# Revit family: efg_egg-20_60ms(t)b2_60Hz
name_source: partatom
category: 機械設備
units: mm (PartAtom-declared; Revit-internal decimal feet)

## family parameters
OmniClass タイトル = Industrial Ventilating Equipment
OmniClass 番号 = 23.75.35.21.17
パーツ タイプ = 標準
ロード時にボイドで切り取り = はい
丸型コネクタ寸法 = 直径を使用
作業面ベース = いいえ
共有 = いいえ
常に垂直 = はい
部屋計算ポイント = はい

## types (7) — shared parameters
IfcExportAs = IfcFanType
IfcExportType = TUBEAXIAL
MID風量 = 0.0 m³/h
OmniClassCode = 23-33 31 19 11 17
URL = https://www.mitsubishielectric.co.jp
Uniclass2015Code = Pr_65_67_29_67
Uniclass2015Title = Propeller fans
Uniclass2015Version = Systems v1.9
ファンの種類 = 軸流羽根
仕様書バージョン = Version1.0
企業コード = 108420
分類コード = 50052503100110
周波数 = 60 Hz
呼称 = 有圧扇
法定耐用年数 = 15
製品リリース年月 = 2022年6月1日
製品出荷対象 = 国内
製造元 = 三菱電機株式会社
設置方法 = 壁付
説明 = 業務用有圧換気扇 店舗用 メッシュタイプ 排気形
負荷分類 = 3_ファン類
運転質量 = 0.00 kg

## per-type parameters (varying)
| type | D1 | Depth | H1 | Height | MAX風量 | MIN風量 | W1 | Width | 価格 | 極 | 極数 | 消費電力 | 番手 | 相 | 製品質量 | 質量 | 電動機出力 | 電圧 |
| EFG-25MSB2 | 155  [stored 0.50853 ft] | 247 | 294  [stored 0.964567 ft] | 374  [stored 1.22703 ft] | 1130.0 m³/h | 870.0 m³/h | 294  [stored 0.964567 ft] | 379  [stored 1.24344 ft] | 68600 $ | 4 | 2 | 41 W | ∅250 | 1 | 6.10 kg | 7.32 kg | 25 W | 100 V |
| EFG-30MSB2 | 155  [stored 0.50853 ft] | 272 | 344  [stored 1.12861 ft] | 424  [stored 1.39108 ft] | 1720.0 m³/h | 1200.0 m³/h | 344  [stored 1.12861 ft] | 429  [stored 1.40748 ft] | 83500 $ | 4 | 2 | 61 W | ∅300 | 1 | 7.70 kg | 9.24 kg | 50 W | 100 V |
| EFG-35MSB2 | 155  [stored 0.50853 ft] | 277  [stored 0.908793 ft] | 399  [stored 1.30906 ft] | 479  [stored 1.57152 ft] | 2470.0 m³/h | 1810.0 m³/h | 399  [stored 1.30906 ft] | 484  [stored 1.58793 ft] | 121000 $ | 4 | 2 | 110 W | ∅350 | 1 | 10.60 kg | 12.72 kg | 100 W | 100 V |
| EFG-40MSB2 | 159  [stored 0.521654 ft] | 343  [stored 1.12533 ft] | 423  [stored 1.3878 ft] | 518  [stored 1.69948 ft] | 3460.0 m³/h | 2600.0 m³/h | 423  [stored 1.3878 ft] | 520  [stored 1.70604 ft] | 156000 $ | 4 | 2 | 177 W | ∅400 | 1 | 17.10 kg | 20.52 kg | 150 W | 100 V |
| EFG-40MSTB2 | 159  [stored 0.521654 ft] | 343  [stored 1.12533 ft] | 423  [stored 1.3878 ft] | 518  [stored 1.69948 ft] | 3420.0 m³/h | 0.0 m³/h | 423  [stored 1.3878 ft] | 520  [stored 1.70604 ft] | 156000 $ | 4 | 3 | 164 W | ∅400 | 3 | 16.90 kg | 20.28 kg | 150 W | 200 V |
| EGG-50MSTB2 | 189  [stored 0.620079 ft] | 413  [stored 1.35499 ft] | 524  [stored 1.71916 ft] | 618  [stored 2.02756 ft] | 5840.0 m³/h | 0.0 m³/h | 524  [stored 1.71916 ft] | 620  [stored 2.03412 ft] | 201000 $ | 6 | 3 | 310 W | ∅500 | 3 | 25.30 kg | 30.36 kg | 400 W | 200 V |
| EGG-60MSTB2 | 189  [stored 0.620079 ft] | 433 | 614  [stored 2.01444 ft] | 708  [stored 2.32283 ft] | 8530.0 m³/h | 0.0 m³/h | 614  [stored 2.01444 ft] | 710 | 265000 $ | 6 | 3 | 460 W | ∅600 | 3 | 30.70 kg | 36.84 kg | 400 W | 200 V |

note: column(s) folded — value = type name in every type: モデル

note: [stored X ft] marks values corroborated as IEEE doubles in the binary element streams (Revit-internal decimal feet)
